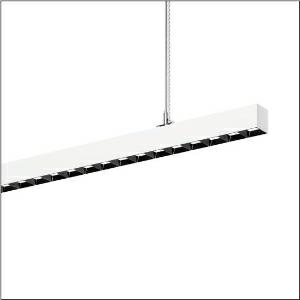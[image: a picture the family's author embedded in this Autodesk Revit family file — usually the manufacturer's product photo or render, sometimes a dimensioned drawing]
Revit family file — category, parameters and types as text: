
# Revit family: silica_r__21_51mx32dc4dwb_0a61
name_source: partatom
category: Lighting Fixtures
units: mm (PartAtom-declared; Revit-internal decimal feet)

## family parameters
Cut with Voids When Loaded = No
Host = Face
Light Source = No
Part Type = Normal
Room Calculation Point = No
Round Connector Dimension = Use Diameter
Shared = No

## types (1)
- --- (1 x LED, 18230 lm, 105.8 W, 4000K)
    Apparent Load = 106 VA
    CIE Flux Codes = 86 99 100 59 100
    Color Rendering = 80
    Color Temperature = 4000K
    Default Elevation = 1800 mm
    Description = Silica® 21, office luminaire, primary light control with darklight reflector, of PMMA, black, CAT 2 (L<= 3000cd/m²), light emission: direct/indirect distribution, primary light characteristic: symmetric, installation type: suspended mounting, LED, rated luminous flux: 18.230lm, luminous efficacy: 172lm/W, light colour: 840, colour temperature: 4000K, control gear: DALI 2, with terminal, 3+2-pole, max. 2.5mm², mains connection: 220..240V, AC, 50/60Hz, rated input power: 105.8W, luminaire housing, of aluminium, traffic white (RAL 9016), length: 3.004mm, width: 53mm, height: 53mm, protection rating (complete): IP20, insulation class (complete): insulation class I (protective earthing), certification: CE, permissible operating ambient temperature: 0..+35°C, standard: EN 50419, packaging unit: 1 piece
    Height = 53 mm
    Lamp = 1 x LED
    Lamp Light Flux = 18230 lm
    Lamp Power = 105.8 W
    Lamp count = 1
    Length = 3004 mm
    Luminous efficacy = 172 lm/W
    Manufacturer = Siteco
    ModVariant = No
    Model = 51MX32DC4DWB
    Mounting Place = Ceiling
    Mounting Type = Pendant
    Number of Poles = 1
    OnlyDefault = Yes
    Power Factor = 1
    Product Name = Silica® 21
    Product group = office luminaire | ceiling pendant
    ProductGroupID = 903
    Protection Class = Protection class I
    Protection Degree = IP 20
    RLX_Detail_Level = 1
    RLX_Emergency_Light_Flux = 0 lm
    RLX_Emergency_Type = 0
    RLX_Emergency_Type_DB = No
    RlxData = <blob elided: 64581 chars, md5=cc8e4911>
    Socket = socket
    Standby Power = 0 W
    System Light Flux = 18230 lm
    System Power = 106 W
    Type Comments = factory setting: luminous flux: 100 % | dim-lin: 254 | 366 mA
    Type Image = l_1335871.jpg
    URL = http://relux.com
    VarID = @adj_143757
    Voltage = 0 V
    Weight = 0.00 kg
    Width = 53 mm

## geometry (parser evidence)
native form markers: Blend x4, Sweep x10
no freeform markers — native parametric forms only
